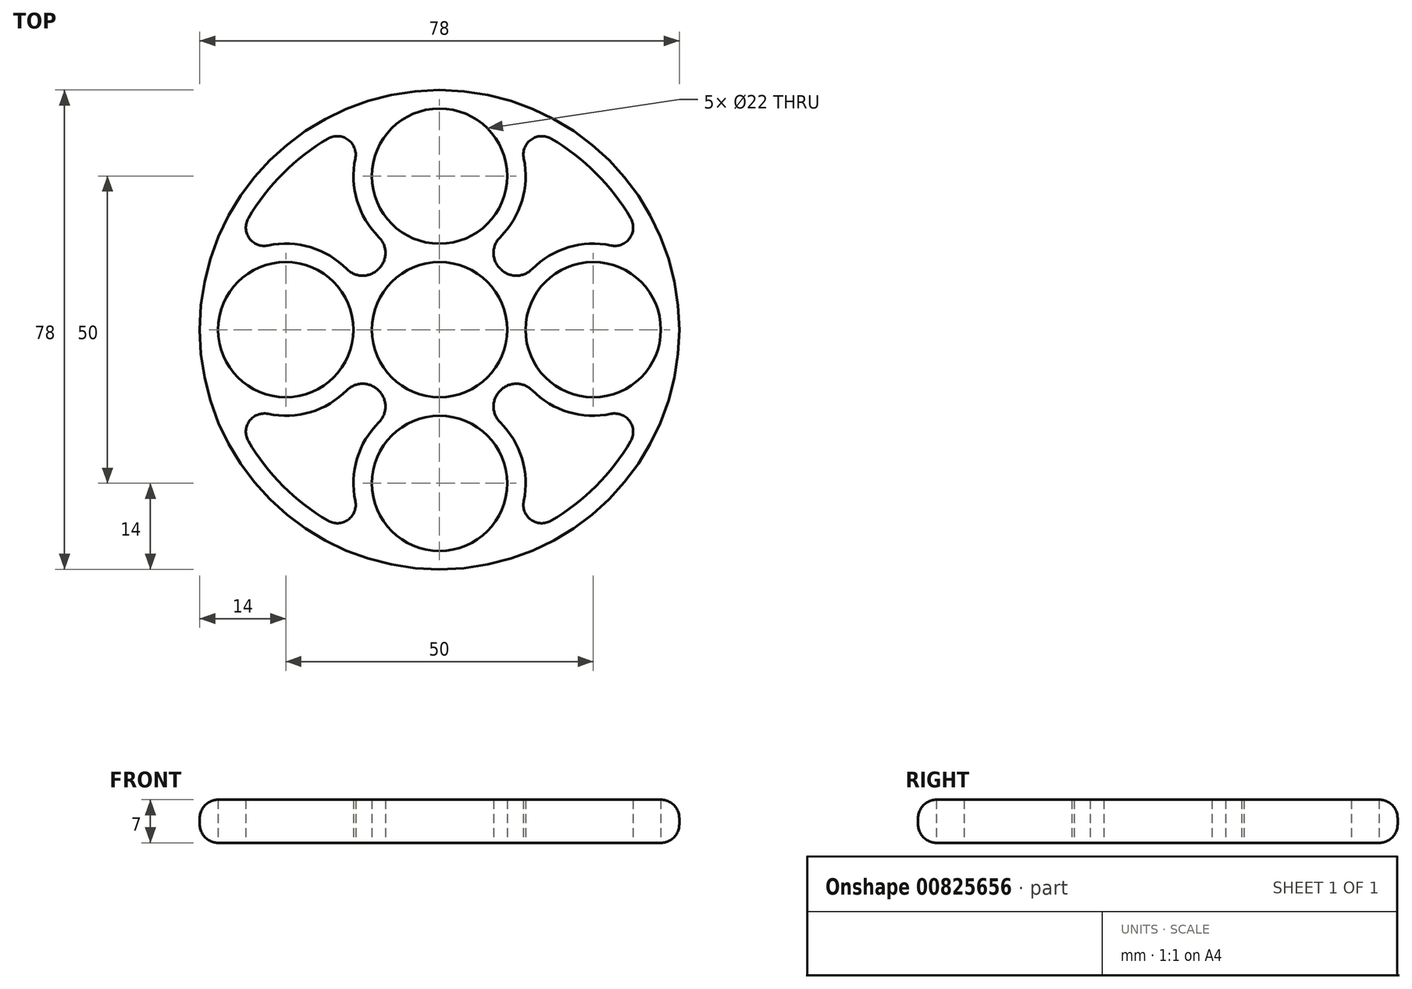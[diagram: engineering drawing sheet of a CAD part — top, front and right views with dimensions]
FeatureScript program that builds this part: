
annotation { "Feature Type Name" : "Feature", "Feature Type Description" : "" }
export const myFeature = defineFeature(function(context is Context, id is Id, definition is map)
    precondition{}
    {
        {
            var Q0;
            Q0=qCreatedBy(makeId("Top.planeOp"),FACE);
            var sketch = newSketch(context, id + "F0", { "sketchPlane" : qUnion([Q0])});
            skCircle(sketch, "E0", {"center": v(0, 0) * mm, "radius": 39 * mm});
            skLineSegment(sketch, "E1", {"start": v(0, 0) * mm, "end": v(39, 0) * mm, "construction": true});
            skCircle(sketch, "E2", {"center": v(0, 0) * mm, "radius": 11 * mm});
            skCircle(sketch, "E3", {"center": v(0, 25) * mm, "radius": 11 * mm});
            skLineSegment(sketch, "E4", {"start": v(-39, 0) * mm, "end": v(0, 0) * mm, "construction": true});
            skLineSegment(sketch, "E5", {"start": v(0, -39) * mm, "end": v(0, 0) * mm, "construction": true});
            skLineSegment(sketch, "E6", {"start": v(0, 0) * mm, "end": v(0, 39) * mm, "construction": true});
            skCircle(sketch, "E7.1.0", {"center": v(-25, 0) * mm, "radius": 11 * mm});
            skCircle(sketch, "E7.2.0", {"center": v(0, -25) * mm, "radius": 11 * mm});
            skCircle(sketch, "E7.3.0", {"center": v(25, 0) * mm, "radius": 11 * mm});
            skArc(sketch, "E8", {"start": v(9.86, 15.06) * mm, "mid": v(13.41, 20.98) * mm, "end": v(13.7, 27.88) * mm});
            skArc(sketch, "E9", {"start": v(15.06, -9.86) * mm, "mid": v(20.98, -13.41) * mm, "end": v(27.88, -13.7) * mm});
            skArc(sketch, "E10", {"start": v(-9.86, -15.06) * mm, "mid": v(-13.41, -20.98) * mm, "end": v(-13.7, -27.88) * mm});
            skArc(sketch, "E11", {"start": v(-15.06, 9.86) * mm, "mid": v(-20.98, 13.41) * mm, "end": v(-27.88, 13.7) * mm});
            skArc(sketch, "E12", {"start": v(-9.86, 9.94) * mm, "mid": v(-9.9, 9.9) * mm, "end": v(-9.94, 9.86) * mm});
            skArc(sketch, "E13.trimOffspring", {"start": v(-9.94, -9.86) * mm, "mid": v(-9.9, -9.9) * mm, "end": v(-9.86, -9.94) * mm});
            skArc(sketch, "E14.trimOffspring", {"start": v(9.86, -9.94) * mm, "mid": v(9.9, -9.9) * mm, "end": v(9.94, -9.86) * mm});
            skArc(sketch, "E15.trimOffspring", {"start": v(9.94, 9.86) * mm, "mid": v(9.9, 9.9) * mm, "end": v(9.86, 9.94) * mm});
            skPoint(sketch, "E16.visualSharp", {"position": v(6.3, 12.5) * mm});
            skArc(sketch, "E16.filletArc", {"start": v(9.86, 15.06) * mm, "mid": v(8.79, 12.5) * mm, "end": v(9.86, 9.94) * mm});
            skPoint(sketch, "E17.visualSharp", {"position": v(12.5, 6.3) * mm});
            skArc(sketch, "E17.filletArc", {"start": v(9.94, 9.86) * mm, "mid": v(12.5, 8.79) * mm, "end": v(15.06, 9.86) * mm});
            skPoint(sketch, "E18.visualSharp", {"position": v(-6.3, 12.5) * mm});
            skArc(sketch, "E18.filletArc", {"start": v(-9.86, 9.94) * mm, "mid": v(-8.79, 12.5) * mm, "end": v(-9.86, 15.06) * mm});
            skPoint(sketch, "E19.visualSharp", {"position": v(-12.5, 6.3) * mm});
            skArc(sketch, "E19.filletArc", {"start": v(-15.06, 9.86) * mm, "mid": v(-12.5, 8.79) * mm, "end": v(-9.94, 9.86) * mm});
            skPoint(sketch, "E20.visualSharp", {"position": v(-12.5, -6.3) * mm});
            skArc(sketch, "E20.filletArc", {"start": v(-9.94, -9.86) * mm, "mid": v(-12.5, -8.79) * mm, "end": v(-15.06, -9.86) * mm});
            skPoint(sketch, "E21.visualSharp", {"position": v(-6.3, -12.5) * mm});
            skArc(sketch, "E21.filletArc", {"start": v(-9.86, -15.06) * mm, "mid": v(-8.79, -12.5) * mm, "end": v(-9.86, -9.94) * mm});
            skPoint(sketch, "E22.visualSharp", {"position": v(6.3, -12.5) * mm});
            skArc(sketch, "E22.filletArc", {"start": v(9.86, -9.94) * mm, "mid": v(8.79, -12.5) * mm, "end": v(9.86, -15.06) * mm});
            skPoint(sketch, "E23.visualSharp", {"position": v(12.5, -6.3) * mm});
            skArc(sketch, "E23.filletArc", {"start": v(15.06, -9.86) * mm, "mid": v(12.5, -8.79) * mm, "end": v(9.94, -9.86) * mm});
            skArc(sketch, "E24", {"start": v(-18.15, 31.1) * mm, "mid": v(-25.46, 25.46) * mm, "end": v(-31.1, 18.15) * mm});
            skArc(sketch, "E25.trimOffspring", {"start": v(-13.7, 27.88) * mm, "mid": v(-13.41, 20.98) * mm, "end": v(-9.86, 15.06) * mm});
            skArc(sketch, "E26.trimOffspring", {"start": v(27.88, 13.7) * mm, "mid": v(20.98, 13.41) * mm, "end": v(15.06, 9.86) * mm});
            skArc(sketch, "E27.trimOffspring", {"start": v(31.1, 18.15) * mm, "mid": v(25.46, 25.46) * mm, "end": v(18.15, 31.1) * mm});
            skArc(sketch, "E28.trimOffspring", {"start": v(13.7, -27.88) * mm, "mid": v(13.41, -20.98) * mm, "end": v(9.86, -15.06) * mm});
            skArc(sketch, "E29.trimOffspring", {"start": v(18.15, -31.1) * mm, "mid": v(25.46, -25.46) * mm, "end": v(31.1, -18.15) * mm});
            skArc(sketch, "E30.trimOffspring", {"start": v(-27.88, -13.7) * mm, "mid": v(-20.98, -13.41) * mm, "end": v(-15.06, -9.86) * mm});
            skArc(sketch, "E31.trimOffspring", {"start": v(-31.1, -18.15) * mm, "mid": v(-25.46, -25.46) * mm, "end": v(-18.15, -31.1) * mm});
            skPoint(sketch, "E32.visualSharp", {"position": v(-10.28, 34.5) * mm});
            skArc(sketch, "E32.filletArc", {"start": v(-13.7, 27.88) * mm, "mid": v(-14.88, 30.93) * mm, "end": v(-18.15, 31.1) * mm});
            skPoint(sketch, "E33.visualSharp", {"position": v(-34.5, 10.28) * mm});
            skArc(sketch, "E33.filletArc", {"start": v(-31.1, 18.15) * mm, "mid": v(-30.93, 14.88) * mm, "end": v(-27.88, 13.7) * mm});
            skPoint(sketch, "E34.visualSharp", {"position": v(10.28, 34.5) * mm});
            skArc(sketch, "E34.filletArc", {"start": v(18.15, 31.1) * mm, "mid": v(14.88, 30.93) * mm, "end": v(13.7, 27.88) * mm});
            skPoint(sketch, "E35.visualSharp", {"position": v(34.5, 10.28) * mm});
            skArc(sketch, "E35.filletArc", {"start": v(27.88, 13.7) * mm, "mid": v(30.93, 14.88) * mm, "end": v(31.1, 18.15) * mm});
            skPoint(sketch, "E36.visualSharp", {"position": v(-34.5, -10.28) * mm});
            skArc(sketch, "E36.filletArc", {"start": v(-27.88, -13.7) * mm, "mid": v(-30.93, -14.88) * mm, "end": v(-31.1, -18.15) * mm});
            skPoint(sketch, "E37.visualSharp", {"position": v(-10.28, -34.5) * mm});
            skArc(sketch, "E37.filletArc", {"start": v(-18.15, -31.1) * mm, "mid": v(-14.88, -30.93) * mm, "end": v(-13.7, -27.88) * mm});
            skPoint(sketch, "E38.visualSharp", {"position": v(10.28, -34.5) * mm});
            skArc(sketch, "E38.filletArc", {"start": v(13.7, -27.88) * mm, "mid": v(14.88, -30.93) * mm, "end": v(18.15, -31.1) * mm});
            skPoint(sketch, "E39.visualSharp", {"position": v(34.5, -10.28) * mm});
            skArc(sketch, "E39.filletArc", {"start": v(31.1, -18.15) * mm, "mid": v(30.93, -14.88) * mm, "end": v(27.88, -13.7) * mm});
            skSolve(sketch);
        }
        {
            var Q0;
            Q0=makeQuery(id+"F0.imprint","IMPRINT",FACE,{"disambiguationData":[TD([[makeQuery(id+"F0.imprint","IMPRINT",EDGE,{"derivedFrom":sQuery(id+"F0.wireOp",EDGE,"E0")}),1.0]])]});
            extrude(context, id + "F1", {"entities" : qUnion([Q0]), "depth" : 7 * mm, "offsetDistance" : 25 * mm});
        }
        {
            var Q0;
            Q0=makeQuery(id+"F1.opExtrude","SWEPT_FACE",FACE,{"disambiguationData":[OSD([sQuery(id+"F0.wireOp",EDGE,"E0")])]});
            fillet(context, id + "F2", {"entities" : qUnion([Q0]), "radius" : 3 * mm, "tangentPropagation" : true, "allowEdgeOverflow" : false});
        }
    });
